# Revit family: HVAC-Condenser_Res
name_source: partatom
category: Mechanical Equipment
units: mm (PartAtom-declared; Revit-internal decimal feet)

## family parameters
Always vertical = Yes
Classification Number = 23.75.10.24.21.11
Cut with Voids When Loaded = No
Maintain Annotation Orientation = No
Part Type = Normal
Room Calculation Point = No
Round Connector Dimension = Use Diameter
Shared = No
Work Plane-Based = Yes

## types (4) — shared parameters
Assembly Code = D3030
Case Material = ARCAT - Metal - Aluminum - Tan
Compressor Type = Scroll
Construction Details = http://www.arcat.com
Default Elevation = 4' - 0"
Depth = 2' - 0"
Expected Lifespan (Years) = 15
Green Building-LEED = http://www.arcat.com
Height = 2' - 6"
Intake Material = ARCAT - Steel Rod - Chrome Plated
Keynote = 15670
Maintenance Schedule (Months) = 12
Manufacturer = Generic
Manufacturer Fax = (203) 939-2444
Manufacturer Website = http://www.arcat.com
Model = Generic
Product Data = http://www.arcat.com
Product Properties = http://www.arcat.com
Refrigerant = ARCAT - Refrigerant - R 410A
Riser Height = 0' - 4 1/2"
SEER Rating = 15
Sound Level (dB) = 60
Specification = http://www.arcat.com
Warranty Duration (Years) = 10
Width = 2' - 0"

## per-type parameters (varying)
| type | Description |
| 1 Ton | Residential HVAC Condensing Unit - 1 Ton |
| 1.5 Ton | Residential HVAC Condensing Unit - 1.5 Ton |
| 2 Ton | Residential HVAC Condensing Unit - 2 Ton |
| 3 Ton | Residential HVAC Condensing Unit - 3 Ton |

## geometry (parser evidence)
native form markers: Sweep x3
no freeform markers — native parametric forms only
